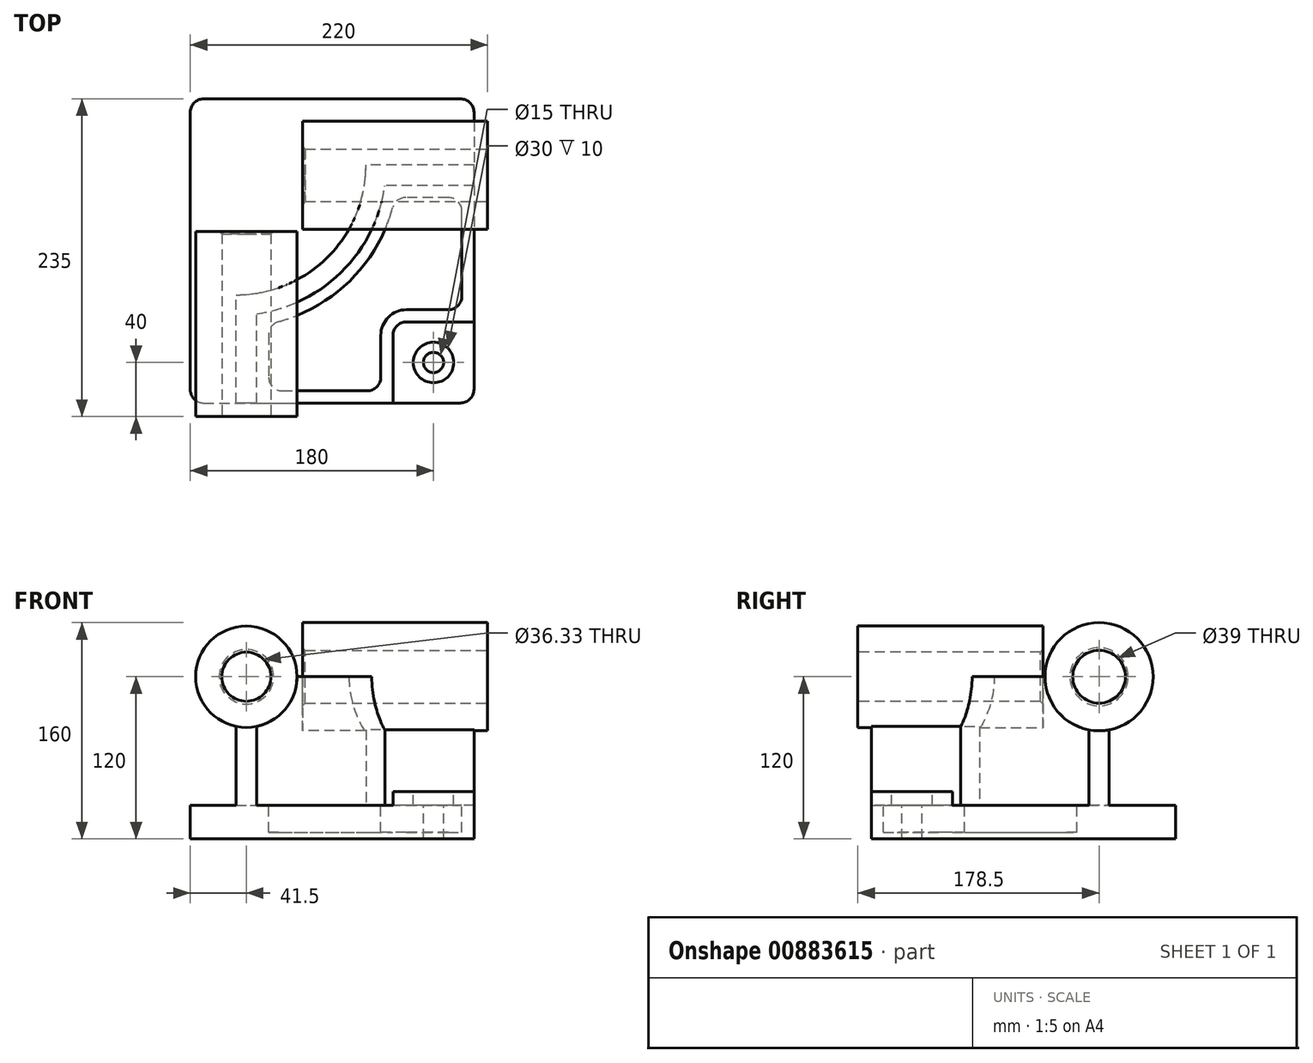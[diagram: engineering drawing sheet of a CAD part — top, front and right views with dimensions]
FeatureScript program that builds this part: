
annotation { "Feature Type Name" : "Feature", "Feature Type Description" : "" }
export const myFeature = defineFeature(function(context is Context, id is Id, definition is map)
    precondition{}
    {
        {
            var Q0;
            Q0=qCreatedBy(makeId("Top.planeOp"),FACE);
            var sketch = newSketch(context, id + "F0", { "sketchPlane" : qUnion([Q0])});
            skLineSegment(sketch, "E0.bottom", {"start": v(-105, 112.5) * mm, "end": v(105, 112.5) * mm});
            skLineSegment(sketch, "E0.top", {"start": v(-105, -112.5) * mm, "end": v(105, -112.5) * mm});
            skLineSegment(sketch, "E0.left", {"start": v(-105, 112.5) * mm, "end": v(-105, -112.5) * mm});
            skLineSegment(sketch, "E0.right", {"start": v(105, 112.5) * mm, "end": v(105, -112.5) * mm});
            skPoint(sketch, "E0.middle", {"position": v(0, 0) * mm});
            skSolve(sketch);
        }
        {
            var Q0;
            Q0 = qSketchRegion(id + "F0", true);
            extrude(context, id + "F1", {"entities" : qUnion([Q0]), "depth" : 25 * mm, "offsetDistance" : 25.4 * mm});
        }
        {
            var Q0;
            Q0=makeQuery(id+"F1.opExtrude","CAP_FACE",FACE,{"disambiguationData":[OSD([sQuery(id+"F0.wireOp",EDGE,"E0.bottom"),sQuery(id+"F0.wireOp",EDGE,"E0.top"),sQuery(id+"F0.wireOp",EDGE,"E0.left"),sQuery(id+"F0.wireOp",EDGE,"E0.right")])],"isStart":false});
            var sketch = newSketch(context, id + "F2", { "sketchPlane" : qUnion([Q0])});
            skLineSegment(sketch, "E1", {"start": v(-71, -112.5) * mm, "end": v(-71, -32.5) * mm});
            skLineSegment(sketch, "E2", {"start": v(105, 63.5) * mm, "end": v(25, 63.5) * mm});
            skArc(sketch, "E3", {"start": v(-71, -32.5) * mm, "mid": v(-3.12, -4.38) * mm, "end": v(25, 63.5) * mm});
            skLineSegment(sketch, "E4", {"start": v(-71, 63.5) * mm, "end": v(-71, -32.5) * mm, "construction": true});
            skLineSegment(sketch, "E5", {"start": v(-71, 63.5) * mm, "end": v(25, 63.5) * mm, "construction": true});
            skLineSegment(sketch, "E6.0", {"start": v(-56, -112.5) * mm, "end": v(-56, -46.48) * mm});
            skArc(sketch, "E6.1", {"start": v(-56, -46.48) * mm, "mid": v(7.49, -14.99) * mm, "end": v(38.98, 48.5) * mm});
            skLineSegment(sketch, "E6.2", {"start": v(105, 48.5) * mm, "end": v(38.98, 48.5) * mm});
            skLineSegment(sketch, "E7.0", {"start": v(105, 112.5) * mm, "end": v(105, -112.5) * mm});
            skLineSegment(sketch, "E8.0", {"start": v(-105, -112.5) * mm, "end": v(105, -112.5) * mm});
            skSolve(sketch);
        }
        {
            var Q0;
            {var subQ2=sQuery(id+"F2.wireOp",EDGE,"E1");Q0=makeQuery(id+"F2.imprint","IMPRINT",FACE,{"disambiguationData":[TD([[makeQuery(id+"F2.imprint","IMPRINT",EDGE,{"derivedFrom":subQ2}),-1.0]])]});}
            extrude(context, id + "F3", {"entities" : qUnion([Q0]), "operationType" : NewBodyOperationType.ADD, "depth" : 95 * mm, "offsetDistance" : 25.4 * mm});
        }
        {
            var Q0;
            Q0=makeQuery(id+"F3.boolean.opBoolean","MERGE",FACE,{"derivedFrom":[makeQuery(id+"F1.opExtrude","SWEPT_FACE",FACE,{"disambiguationData":[OSD([sQuery(id+"F0.wireOp",EDGE,"E0.top")])]}),makeQuery(id+"F3.opExtrude","SWEPT_FACE",FACE,{"disambiguationData":[OSD([sQuery(id+"F2.wireOp",EDGE,"E8.0")])]})]});
            var sketch = newSketch(context, id + "F4", { "sketchPlane" : qUnion([Q0])});
            skCircle(sketch, "E9", {"center": v(-63.5, 120) * mm, "radius": 37.5 * mm});
            skSolve(sketch);
        }
        {
            var Q0;
            Q0 = qSketchRegion(id + "F4", true);
            extrude(context, id + "F5", {"entities" : qUnion([Q0]), "operationType" : NewBodyOperationType.ADD, "depth" : 10 * mm, "offsetDistance" : 25.4 * mm, "hasSecondDirection" : true, "secondDirectionOppositeDirection" : true, "secondDirectionDepth" : (137 - 10) * mm});
        }
        {
            var Q0;
            Q0=makeQuery(id+"F3.boolean.opBoolean","MERGE",FACE,{"derivedFrom":[makeQuery(id+"F1.opExtrude","SWEPT_FACE",FACE,{"disambiguationData":[OSD([sQuery(id+"F0.wireOp",EDGE,"E0.right")])]}),makeQuery(id+"F3.opExtrude","SWEPT_FACE",FACE,{"disambiguationData":[OSD([sQuery(id+"F2.wireOp",EDGE,"E7.0")])]})]});
            var sketch = newSketch(context, id + "F6", { "sketchPlane" : qUnion([Q0])});
            skCircle(sketch, "E10", {"center": v(56, 120) * mm, "radius": 40 * mm});
            skSolve(sketch);
        }
        {
            var Q0;
            {var subQ1=sQuery(id+"F2.wireOp",EDGE,"E7.0");var subQ6=makeQuery(id+"F3.opExtrude","CAP_EDGE",EDGE,{"disambiguationData":[OSD([subQ1])],"isStart":false});Q0=makeQuery(id+"F6.imprint","IMPRINT",FACE,{"disambiguationData":[TD([[makeQuery(id+"F6.imprint","IMPRINT",EDGE,{"derivedFrom":subQ6}),-1.0]])]});}
            var Q1;
            {var subQ1=sQuery(id+"F2.wireOp",EDGE,"E7.0");var subQ6=makeQuery(id+"F3.opExtrude","CAP_EDGE",EDGE,{"disambiguationData":[OSD([subQ1])],"isStart":false});Q1=makeQuery(id+"F6.imprint","IMPRINT",FACE,{"disambiguationData":[TD([[makeQuery(id+"F6.imprint","IMPRINT",EDGE,{"derivedFrom":subQ6}),1.0]])]});}
            extrude(context, id + "F7", {"entities" : qUnion([Q0, Q1]), "operationType" : NewBodyOperationType.ADD, "depth" : 10 * mm, "offsetDistance" : 25.4 * mm, "hasSecondDirection" : true, "secondDirectionOppositeDirection" : true, "secondDirectionDepth" : (137 - 10) * mm});
        }
        {
            var Q0;
            {var subQ0=sQuery(id+"F0.wireOp",EDGE,"E0.right");var subQ1=sQuery(id+"F0.wireOp",EDGE,"E0.top");Q0=makeQuery(id+"F3.boolean.opBoolean","SPLIT",FACE,{"disambiguationData":[TD([makeQuery(id+"F3.opExtrude","SWEPT_FACE",FACE,{"disambiguationData":[OSD([sQuery(id+"F2.wireOp",EDGE,"E6.0")])]})])],"derivedFrom":makeQuery(id+"F1.opExtrude","CAP_FACE",FACE,{"disambiguationData":[OSD([sQuery(id+"F0.wireOp",EDGE,"E0.bottom"),subQ1,sQuery(id+"F0.wireOp",EDGE,"E0.left"),subQ0])],"isStart":false})});}
            var sketch = newSketch(context, id + "F8", { "sketchPlane" : qUnion([Q0])});
            skLineSegment(sketch, "E11.bottom", {"start": v(105, -112.5) * mm, "end": v(45, -112.5) * mm});
            skLineSegment(sketch, "E11.top", {"start": v(105, -52.5) * mm, "end": v(45, -52.5) * mm});
            skLineSegment(sketch, "E11.left", {"start": v(105, -112.5) * mm, "end": v(105, -52.5) * mm});
            skLineSegment(sketch, "E11.right", {"start": v(45, -112.5) * mm, "end": v(45, -52.5) * mm});
            skSolve(sketch);
        }
        {
            var Q0;
            Q0=makeQuery(id+"F8.imprint","IMPRINT",FACE,{"disambiguationData":[TD([[makeQuery(id+"F8.imprint","IMPRINT",EDGE,{"derivedFrom":sQuery(id+"F8.wireOp",EDGE,"E11.bottom")}),1.0]])]});
            extrude(context, id + "F9", {"entities" : qUnion([Q0]), "operationType" : NewBodyOperationType.ADD, "depth" : (35 - 25) * mm, "offsetDistance" : 25.4 * mm});
        }
        {
            var Q0;
            Q0=makeQuery(id+"F9.opExtrude","SWEPT_EDGE",EDGE,{"disambiguationData":[OSD([sQuery(id+"F8.wireOp",EDGE,"E11.top"),sQuery(id+"F8.wireOp",EDGE,"E11.right")])]});
            fillet(context, id + "F10", {"entities" : qUnion([Q0]), "radius" : 10 * mm, "tangentPropagation" : true, "allowEdgeOverflow" : false});
        }
        {
            var Q0;
            {var subQ0=sQuery(id+"F0.wireOp",EDGE,"E0.right");var subQ1=sQuery(id+"F0.wireOp",EDGE,"E0.top");Q0=makeQuery(id+"F3.boolean.opBoolean","SPLIT",FACE,{"disambiguationData":[TD([makeQuery(id+"F3.opExtrude","SWEPT_FACE",FACE,{"disambiguationData":[OSD([sQuery(id+"F2.wireOp",EDGE,"E6.0")])]})])],"derivedFrom":makeQuery(id+"F1.opExtrude","CAP_FACE",FACE,{"disambiguationData":[OSD([sQuery(id+"F0.wireOp",EDGE,"E0.bottom"),subQ1,sQuery(id+"F0.wireOp",EDGE,"E0.left"),subQ0])],"isStart":false})});}
            var sketch = newSketch(context, id + "F11", { "sketchPlane" : qUnion([Q0])});
            skLineSegment(sketch, "E12.0", {"start": v(-47, -54.08) * mm, "end": v(-47, -103.5) * mm});
            skArc(sketch, "E12.1", {"start": v(46.58, 39.5) * mm, "mid": v(13.85, -21.35) * mm, "end": v(-47, -54.08) * mm});
            skLineSegment(sketch, "E12.2", {"start": v(-47, -103.5) * mm, "end": v(36, -103.5) * mm});
            skLineSegment(sketch, "E12.3", {"start": v(96, 39.5) * mm, "end": v(46.58, 39.5) * mm});
            skLineSegment(sketch, "E12.4", {"start": v(36, -103.5) * mm, "end": v(36, -62.5) * mm});
            skArc(sketch, "E12.5", {"start": v(36, -62.5) * mm, "mid": v(41.56, -49.06) * mm, "end": v(55, -43.5) * mm});
            skLineSegment(sketch, "E12.6", {"start": v(55, -43.5) * mm, "end": v(96, -43.5) * mm});
            skLineSegment(sketch, "E12.7", {"start": v(96, -43.5) * mm, "end": v(96, 39.5) * mm});
            skSolve(sketch);
        }
        {
            var Q0;
            Q0=makeQuery(id+"F11.imprint","IMPRINT",FACE,{"disambiguationData":[TD([[makeQuery(id+"F11.imprint","IMPRINT",EDGE,{"derivedFrom":sQuery(id+"F11.wireOp",EDGE,"E12.0")}),1.0]])]});
            extrude(context, id + "F12", {"entities" : qUnion([Q0]), "operationType" : NewBodyOperationType.REMOVE, "oppositeDirection" : true, "depth" : (25 - 5) * mm, "offsetDistance" : 25.4 * mm});
        }
        {
            var Q0;
            Q0=makeQuery(id+"F9.opExtrude","CAP_FACE",FACE,{"disambiguationData":[OSD([sQuery(id+"F8.wireOp",EDGE,"E11.bottom"),sQuery(id+"F8.wireOp",EDGE,"E11.top"),sQuery(id+"F8.wireOp",EDGE,"E11.left"),sQuery(id+"F8.wireOp",EDGE,"E11.right")])],"isStart":false});
            var sketch = newSketch(context, id + "F13", { "sketchPlane" : qUnion([Q0])});
            skCircle(sketch, "E13", {"center": v(75, -82.5) * mm, "radius": 15 * mm});
            skSolve(sketch);
        }
        {
            var Q0;
            Q0=sQuery(id+"F13.wireOp",VERTEX,"E13.center");
            var Q1;
            Q1=makeQuery(id+"F1.opExtrude","SWEPT_BODY",BODY,{"disambiguationData":[OSD([sQuery(id+"F0.wireOp",EDGE,"E0.bottom"),sQuery(id+"F0.wireOp",EDGE,"E0.top"),sQuery(id+"F0.wireOp",EDGE,"E0.left"),sQuery(id+"F0.wireOp",EDGE,"E0.right")])]});
            hole(context, id + "F14", {"style" : HoleStyle.C_BORE, "endStyle" : HoleEndStyle.THROUGH, "holeDiameter" : 15 * mm, "cBoreDiameter" : 30 * mm, "cBoreDepth" : 10 * mm, "majorDiameter" : 6.35 * mm, "isTappedThrough" : true, "tappedDepth" : 12.7 * mm, "tapClearance" : 3, "startFromSketch" : true, "locations" : qUnion([Q0]), "scope" : qUnion([Q1])});
        }
        {
            var Q0;
            Q0=makeQuery(id+"F12.boolean.opBoolean","COPY",EDGE,{"derivedFrom":makeQuery(id+"F12.opExtrude","SWEPT_EDGE",EDGE,{"disambiguationData":[OSD([sQuery(id+"F11.wireOp",EDGE,"E12.0"),sQuery(id+"F11.wireOp",EDGE,"E12.1")])]})});
            var Q1;
            Q1=makeQuery(id+"F12.boolean.opBoolean","COPY",EDGE,{"derivedFrom":makeQuery(id+"F12.opExtrude","SWEPT_EDGE",EDGE,{"disambiguationData":[OSD([sQuery(id+"F11.wireOp",EDGE,"E12.0"),sQuery(id+"F11.wireOp",EDGE,"E12.2")])]})});
            var Q2;
            Q2=makeQuery(id+"F12.boolean.opBoolean","COPY",EDGE,{"derivedFrom":makeQuery(id+"F12.opExtrude","SWEPT_EDGE",EDGE,{"disambiguationData":[OSD([sQuery(id+"F11.wireOp",EDGE,"E12.1"),sQuery(id+"F11.wireOp",EDGE,"E12.3")])]})});
            var Q3;
            Q3=makeQuery(id+"F12.boolean.opBoolean","COPY",EDGE,{"derivedFrom":makeQuery(id+"F12.opExtrude","SWEPT_EDGE",EDGE,{"disambiguationData":[OSD([sQuery(id+"F11.wireOp",EDGE,"E12.3"),sQuery(id+"F11.wireOp",EDGE,"E12.7")])]})});
            var Q4;
            Q4=makeQuery(id+"F12.boolean.opBoolean","COPY",EDGE,{"derivedFrom":makeQuery(id+"F12.opExtrude","SWEPT_EDGE",EDGE,{"disambiguationData":[OSD([sQuery(id+"F11.wireOp",EDGE,"E12.6"),sQuery(id+"F11.wireOp",EDGE,"E12.7")])]})});
            var Q5;
            Q5=makeQuery(id+"F12.boolean.opBoolean","COPY",EDGE,{"derivedFrom":makeQuery(id+"F12.opExtrude","SWEPT_EDGE",EDGE,{"disambiguationData":[OSD([sQuery(id+"F11.wireOp",EDGE,"E12.2"),sQuery(id+"F11.wireOp",EDGE,"E12.4")])]})});
            fillet(context, id + "F15", {"entities" : qUnion([Q0, Q1, Q2, Q3, Q4, Q5]), "radius" : 10 * mm, "tangentPropagation" : true, "allowEdgeOverflow" : false});
        }
        {
            var Q0;
            Q0=makeQuery(id+"F5.opExtrude","CAP_FACE",FACE,{"disambiguationData":[OSD([sQuery(id+"F4.wireOp",EDGE,"E9")])],"isStart":false});
            var sketch = newSketch(context, id + "F16", { "sketchPlane" : qUnion([Q0])});
            skCircle(sketch, "E14", {"center": v(-63.5, 120) * mm, "radius": 18.16 * mm});
            skSolve(sketch);
        }
        {
            var Q0;
            Q0=makeQuery(id+"F16.imprint","IMPRINT",FACE,{"disambiguationData":[TD([[makeQuery(id+"F16.imprint","IMPRINT",EDGE,{"derivedFrom":sQuery(id+"F16.wireOp",EDGE,"E14")}),1.0]])]});
            extrude(context, id + "F17", {"entities" : qUnion([Q0]), "operationType" : NewBodyOperationType.REMOVE, "endBound" : BoundingType.THROUGH_ALL, "oppositeDirection" : true, "depth" : 25.4 * mm, "offsetDistance" : 25.4 * mm});
        }
        {
            var Q0;
            Q0=makeQuery(id+"F7.opExtrude","CAP_FACE",FACE,{"disambiguationData":[OSD([sQuery(id+"F6.wireOp",EDGE,"E10")])],"isStart":false});
            var sketch = newSketch(context, id + "F18", { "sketchPlane" : qUnion([Q0])});
            skCircle(sketch, "E15", {"center": v(56, 120) * mm, "radius": 19.5 * mm});
            skSolve(sketch);
        }
        {
            var Q0;
            Q0=makeQuery(id+"F18.imprint","IMPRINT",FACE,{"disambiguationData":[TD([[makeQuery(id+"F18.imprint","IMPRINT",EDGE,{"derivedFrom":sQuery(id+"F18.wireOp",EDGE,"E15")}),1.0]])]});
            extrude(context, id + "F19", {"entities" : qUnion([Q0]), "operationType" : NewBodyOperationType.REMOVE, "endBound" : BoundingType.THROUGH_ALL, "oppositeDirection" : true, "depth" : 25.4 * mm, "offsetDistance" : 25.4 * mm});
        }
        {
            var Q0;
            Q0=makeQuery(id+"F17.boolean.opBoolean","COPY",EDGE,{"derivedFrom":makeQuery(id+"F17.opExtrude","CAP_EDGE",EDGE,{"disambiguationData":[OSD([sQuery(id+"F16.wireOp",EDGE,"E14")])],"isStart":true})});
            var Q1;
            Q1=makeQuery(id+"F19.boolean.opBoolean","COPY",EDGE,{"derivedFrom":makeQuery(id+"F19.opExtrude","CAP_EDGE",EDGE,{"disambiguationData":[OSD([sQuery(id+"F18.wireOp",EDGE,"E15")])],"isStart":true})});
            var Q2;
            Q2=makeQuery(id+"F17.boolean.opBoolean","INTERSECT",EDGE,{"derivedFrom":[makeQuery(id+"F5.opExtrude","CAP_FACE",FACE,{"disambiguationData":[OSD([sQuery(id+"F4.wireOp",EDGE,"E9")])],"isStart":true}),makeQuery(id+"F17.opExtrude","SWEPT_FACE",FACE,{"disambiguationData":[OSD([sQuery(id+"F16.wireOp",EDGE,"E14")])]})]});
            var Q3;
            Q3=makeQuery(id+"F19.boolean.opBoolean","INTERSECT",EDGE,{"derivedFrom":[makeQuery(id+"F7.opExtrude","CAP_FACE",FACE,{"disambiguationData":[OSD([sQuery(id+"F6.wireOp",EDGE,"E10")])],"isStart":true}),makeQuery(id+"F19.opExtrude","SWEPT_FACE",FACE,{"disambiguationData":[OSD([sQuery(id+"F18.wireOp",EDGE,"E15")])]})]});
            chamfer(context, id + "F20", {"entities" : qUnion([Q0, Q1, Q2, Q3]), "width" : 2 * mm, "tangentPropagation" : true});
        }
        {
            var Q0;
            Q0=makeQuery(id+"F9.boolean.opBoolean","MERGE",EDGE,{"derivedFrom":[makeQuery(id+"F1.opExtrude","SWEPT_EDGE",EDGE,{"disambiguationData":[OSD([sQuery(id+"F0.wireOp",EDGE,"E0.top"),sQuery(id+"F0.wireOp",EDGE,"E0.right")])]}),makeQuery(id+"F9.opExtrude","SWEPT_EDGE",EDGE,{"disambiguationData":[OSD([sQuery(id+"F8.wireOp",EDGE,"E11.bottom"),sQuery(id+"F8.wireOp",EDGE,"E11.left")])]})]});
            var Q1;
            Q1=makeQuery(id+"F1.opExtrude","SWEPT_EDGE",EDGE,{"disambiguationData":[OSD([sQuery(id+"F0.wireOp",EDGE,"E0.bottom"),sQuery(id+"F0.wireOp",EDGE,"E0.right")])]});
            var Q2;
            Q2=makeQuery(id+"F1.opExtrude","SWEPT_EDGE",EDGE,{"disambiguationData":[OSD([sQuery(id+"F0.wireOp",EDGE,"E0.bottom"),sQuery(id+"F0.wireOp",EDGE,"E0.left")])]});
            var Q3;
            Q3=makeQuery(id+"F1.opExtrude","SWEPT_EDGE",EDGE,{"disambiguationData":[OSD([sQuery(id+"F0.wireOp",EDGE,"E0.top"),sQuery(id+"F0.wireOp",EDGE,"E0.left")])]});
            fillet(context, id + "F21", {"entities" : qUnion([Q0, Q1, Q2, Q3]), "radius" : 10 * mm, "tangentPropagation" : true, "allowEdgeOverflow" : false});
        }
    });
